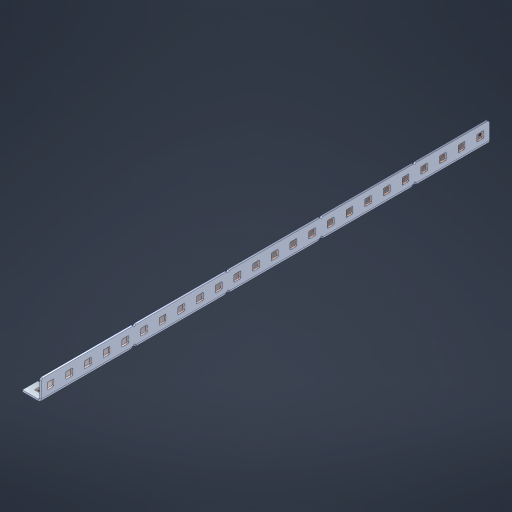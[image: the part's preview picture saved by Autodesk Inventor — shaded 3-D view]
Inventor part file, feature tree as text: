
AUTODESK INVENTOR PART (.ipt)
format: ipt  version: 2023 (Build 270158000, 158)  size: 1,047,552 bytes
history: native  units: in
note: dims shown in document units (in); Inventor stores cm internally (conversion verified against a paired STEP export)
features: other x79, extrude x70, sheet_metal_op x11, sketch x10, pattern_linear x2, mirror x1, chamfer x1
ambient origin geometry x8: Origin, YZ Plane, XZ Plane, XY Plane, X Axis, Y Axis, Z Axis, Center Point
bodies: Solid1 (feature_tree), Body (feature_tree)
feature tree (174):
  sheet_metal_op  "Flanges"
  other  "Flange Pattern Plane"
  other  "Flange Pattern Sketch"
  sheet_metal_op  "Flange Pattern"
  sheet_metal_op  "Body Pattern"
  pattern_linear  "Center Pattern"  Spacing1=0.0469in  [1 undecoded]
  other  "Arc Length"
  mirror  "Notch Mirror"
  pattern_linear  "Notch Pattern"  Spacing1=0.182in  [1 undecoded]
  chamfer  "End Chamfer"
  extrude  "Half Cut"  Depth=0.02in
  sketch  "Sketch1"  dims[d0=1.0in]
  other  "Plate1"
  sketch  "Sketch2"  dims[d1=12.0in]
  other  "Plate2"
  sheet_metal_op  "Bend1"
  sheet_metal_op  "Corner1"
  sketch  "Sketch3"  dims[d2=0.0469in]
  sketch  "Sketch7"  dims[d3=0.0469in]
  other  "Srf1"
  other  "Srf2"
  sketch  "Sketch8"  dims[d4=0.0234in]
  sketch  "Sketch9"  dims[d5=0.0938in]
  other  "Srf91"
  sheet_metal_op  "Body Pattern Sketch"
  other  "Srf92"
  sketch  "Sketch13"  dims[d6=0.0469in]
  sketch  "Sketch14"  dims[d7=0.5in d8=90.0deg d9=0.0312in]
  sketch  "Sketch15"  dims[d10=0.1875in]
  sketch  "Sketch16"  dims[d11=0.0469in d12=0.0469in d16=0.182in d17=0.02in d18=0.0469in d19=0.0in d20=0.25in d21=0.25in d38=9.4488in d40=0.5in d41=0.3937in d43=1.0in d46=0.172in d47=1.0in d48=0.0in d49=0.182in d50=0.02in d51=0.25in d52=0.25in d53=0.0469in d54=0.0in d55=0.172in d56=1.0in d57=0.0in d58=0.25in d60=9.4488in d62=0.5in d63=0.3937in d65=0.5in d85=0.1227in d86=0.1659in d88=0.04in d89=0.0469in d90=0.0in d91=0.04in d92=0.0491in d95=2.5in d96=0.04in d97=0.25in d98=45.0deg d99=0.25in d100=0.5in d101=0.0in d102=2.497in d106=0.182in d107=0.02in d108=0.5in d109=0.5in d110=0.0469in d111=0.0in d112=0.172in d113=0.5in d114=0.0in d117=0.5in d118=0.5in d119=0.5in]
  other  "Srf786"
  other  "Srf823"
  other  "Srf824"
  other  "Srf825"
  other  "Srf826"
  other  "Srf827"
  other  "Srf828"
  other  "Srf829"
  other  "Srf856"
  other  "Srf857"
  other  "Srf858"
  other  "Srf859"
  other  "Srf860"
  other  "Srf861"
  other  "Srf862"
  other  "Srf889"
  other  "Srf890"
  other  "Srf891"
  other  "Srf892"
  other  "Srf893"
  other  "Srf894"
  other  "Srf895"
  other  "Srf896"
  other  "Srf922"
  other  "Srf923"
  other  "Srf924"
  other  "Srf925"
  other  "Srf926"
  other  "Srf959"
  other  "Srf960"
  other  "Srf961"
  other  "Srf962"
  other  "Srf963"
  other  "Srf996"
  other  "Srf997"
  other  "Srf998"
  other  "Srf999"
  other  "Srf1000"
  other  "Srf1143"
  other  "Srf1144"
  other  "Srf1145"
  other  "Srf1146"
  other  "Srf1147"
  other  "Srf1148"
  other  "Srf1149"
  other  "Srf1150"
  other  "Srf1151"
  other  "Srf1152"
  other  "Srf1199"
  other  "Srf1200"
  other  "Srf1201"
  other  "Srf1202"
  other  "Srf1203"
  other  "Srf1204"
  other  "Srf1205"
  other  "Srf1206"
  other  "Srf1207"
  other  "Srf1208"
  other  "Srf1255"
  other  "Srf1256"
  other  "Srf1257"
  other  "Srf1258"
  other  "Srf1259"
  other  "Srf1260"
  other  "Srf1261"
  other  "Srf1262"
  other  "Srf1263"
  other  "Srf1264"
  sheet_metal_op  "Flange Stamp"
  sheet_metal_op  "Flange Circle"
  sheet_metal_op  "Body Stamp"
  sheet_metal_op  "Body Circle"
  other  "Center Stamp"
  other  "Center Circle"
  sheet_metal_op  "Notch"
  extrude  "ExtrusionSrf2"  Depth=0.0469in
  extrude  "ExtrusionSrf92"  TaperAngle=0.0deg  [1 undecoded]
  extrude  "ExtrusionSrf823"  Depth=0.25in
  extrude  "ExtrusionSrf824"  Depth=0.25in
  extrude  "ExtrusionSrf825"  Depth=0.5in
  extrude  "ExtrusionSrf826"  Depth=0.5in
  extrude  "ExtrusionSrf827"  Depth=1.0in TaperAngle=0.0deg
  extrude  "ExtrusionSrf828"  Depth=0.182in
  extrude  "ExtrusionSrf829"  Depth=0.02in
  extrude  "ExtrusionSrf856"  Depth=0.25in
  extrude  "ExtrusionSrf857"  Depth=0.25in
  extrude  "ExtrusionSrf858"  Depth=0.0469in
  extrude  "ExtrusionSrf859"  TaperAngle=0.0deg  [1 undecoded]
  extrude  "ExtrusionSrf860"  Depth=0.5in
  extrude  "ExtrusionSrf861"  Depth=1.0in TaperAngle=0.0deg
  extrude  "ExtrusionSrf862"  Depth=0.25in
  extrude  "ExtrusionSrf889"  Depth=0.5in
  extrude  "ExtrusionSrf890"  Depth=0.5in
  extrude  "ExtrusionSrf891"  Depth=0.5in
  extrude  "ExtrusionSrf892"  Depth=0.5in
  extrude  "ExtrusionSrf893"  Depth=0.5in
  extrude  "ExtrusionSrf894"  Depth=0.0469in
  extrude  "ExtrusionSrf895"  TaperAngle=0.0deg  [1 undecoded]
  extrude  "ExtrusionSrf896"  Depth=0.5in
  extrude  "ExtrusionSrf922"  Depth=0.5in
  extrude  "ExtrusionSrf923"  Depth=2.5in
  extrude  "ExtrusionSrf924"  Depth=0.25in TaperAngle=45.0deg
  extrude  "ExtrusionSrf925"  Depth=0.25in
  extrude  "ExtrusionSrf926"  Depth=0.5in TaperAngle=0.0deg
  extrude  "ExtrusionSrf959"  Depth=0.5in
  extrude  "ExtrusionSrf960"  Depth=0.182in
  extrude  "ExtrusionSrf961"  Depth=0.02in
  extrude  "ExtrusionSrf962"  Depth=0.5in
  extrude  "ExtrusionSrf963"  Depth=0.5in
  extrude  "ExtrusionSrf996"  Depth=0.0469in
  extrude  "ExtrusionSrf997"  TaperAngle=0.0deg  [1 undecoded]
  extrude  "ExtrusionSrf998"  Depth=0.5in
  extrude  "ExtrusionSrf999"  Depth=0.5in TaperAngle=0.0deg
  extrude  "ExtrusionSrf1000"  Depth=0.5in
  extrude  "ExtrusionSrf1143"  Depth=0.5in
  extrude  "ExtrusionSrf1144"  Depth=0.5in
  extrude  "ExtrusionSrf1145"  [1 undecoded]
  extrude  "ExtrusionSrf1146"  [1 undecoded]
  extrude  "ExtrusionSrf1147"  [1 undecoded]
  extrude  "ExtrusionSrf1148"  [1 undecoded]
  extrude  "ExtrusionSrf1149"  [1 undecoded]
  extrude  "ExtrusionSrf1150"  [1 undecoded]
  extrude  "ExtrusionSrf1151"  [1 undecoded]
  extrude  "ExtrusionSrf1152"  [1 undecoded]
  extrude  "ExtrusionSrf1199"  [1 undecoded]
  extrude  "ExtrusionSrf1200"  [1 undecoded]
  extrude  "ExtrusionSrf1201"  [1 undecoded]
  extrude  "ExtrusionSrf1202"  [1 undecoded]
  extrude  "ExtrusionSrf1203"  [1 undecoded]
  extrude  "ExtrusionSrf1204"  [1 undecoded]
  extrude  "ExtrusionSrf1205"  [1 undecoded]
  extrude  "ExtrusionSrf1206"  [1 undecoded]
  extrude  "ExtrusionSrf1207"  [1 undecoded]
  extrude  "ExtrusionSrf1208"  [1 undecoded]
  extrude  "ExtrusionSrf1255"  [1 undecoded]
  extrude  "ExtrusionSrf1256"  [1 undecoded]
  extrude  "ExtrusionSrf1257"  [1 undecoded]
  extrude  "ExtrusionSrf1258"  [1 undecoded]
  extrude  "ExtrusionSrf1259"  [1 undecoded]
  extrude  "ExtrusionSrf1260"  [1 undecoded]
  extrude  "ExtrusionSrf1261"  [1 undecoded]
  extrude  "ExtrusionSrf1262"  [1 undecoded]
  extrude  "ExtrusionSrf1263"  [1 undecoded]
  extrude  "ExtrusionSrf1264"  [1 undecoded]
note: 34 required parameter values undecoded (feature->parameter linkage not recoverable at this tier; creation-order binding heuristic only, values carry confidence <= 0.55)
